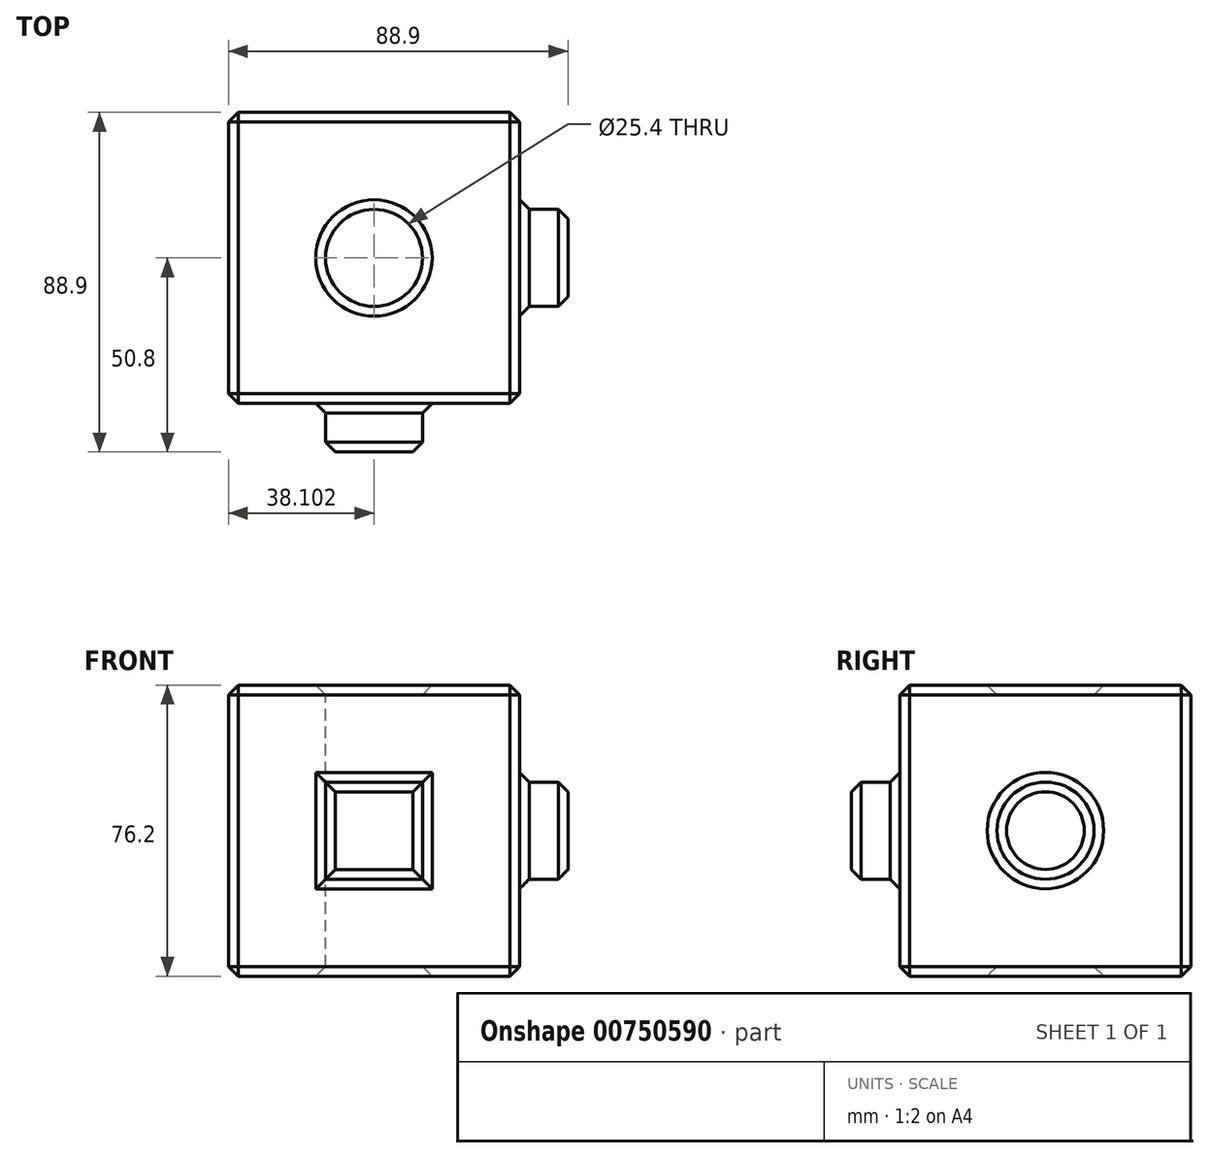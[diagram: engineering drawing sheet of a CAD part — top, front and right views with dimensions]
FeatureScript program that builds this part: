
annotation { "Feature Type Name" : "Feature", "Feature Type Description" : "" }
export const myFeature = defineFeature(function(context is Context, id is Id, definition is map)
    precondition{}
    {
        {
            var Q0;
            Q0=qCreatedBy(makeId("Front.planeOp"),FACE);
            var sketch = newSketch(context, id + "F0", { "sketchPlane" : qUnion([Q0])});
            skLineSegment(sketch, "E0.bottom", {"start": v(-35.36, -32.41) * mm, "end": v(40.84, -32.41) * mm});
            skLineSegment(sketch, "E0.top", {"start": v(-35.36, 43.79) * mm, "end": v(40.84, 43.79) * mm});
            skLineSegment(sketch, "E0.left", {"start": v(-35.36, -32.41) * mm, "end": v(-35.36, 43.79) * mm});
            skLineSegment(sketch, "E0.right", {"start": v(40.84, -32.41) * mm, "end": v(40.84, 43.79) * mm});
            skSolve(sketch);
        }
        {
            var Q0;
            Q0=makeQuery(id+"F0.imprint","IMPRINT",FACE,{"disambiguationData":[TD([[makeQuery(id+"F0.imprint","IMPRINT",EDGE,{"derivedFrom":sQuery(id+"F0.wireOp",EDGE,"E0.bottom")}),1.0]])]});
            extrude(context, id + "F1", {"entities" : qUnion([Q0]), "oppositeDirection" : true, "depth" : 76.2 * mm, "offsetDistance" : 25.4 * mm});
        }
        {
            var Q0;
            Q0=makeQuery(id+"F1.opExtrude","CAP_FACE",FACE,{"disambiguationData":[OSD([sQuery(id+"F0.wireOp",EDGE,"E0.bottom"),sQuery(id+"F0.wireOp",EDGE,"E0.top"),sQuery(id+"F0.wireOp",EDGE,"E0.left"),sQuery(id+"F0.wireOp",EDGE,"E0.right")])],"isStart":true});
            var sketch = newSketch(context, id + "F2", { "sketchPlane" : qUnion([Q0])});
            skLineSegment(sketch, "E1.bottom", {"start": v(-9.96, -7.01) * mm, "end": v(15.44, -7.01) * mm});
            skLineSegment(sketch, "E1.top", {"start": v(-9.96, 18.39) * mm, "end": v(15.44, 18.39) * mm});
            skLineSegment(sketch, "E1.left", {"start": v(-9.96, -7.01) * mm, "end": v(-9.96, 18.39) * mm});
            skLineSegment(sketch, "E1.right", {"start": v(15.44, -7.01) * mm, "end": v(15.44, 18.39) * mm});
            skSolve(sketch);
        }
        {
            var Q0;
            Q0=makeQuery(id+"F2.imprint","IMPRINT",FACE,{"disambiguationData":[TD([[makeQuery(id+"F2.imprint","IMPRINT",EDGE,{"derivedFrom":sQuery(id+"F2.wireOp",EDGE,"E1.bottom")}),1.0]])]});
            extrude(context, id + "F3", {"entities" : qUnion([Q0]), "operationType" : NewBodyOperationType.ADD, "depth" : 12.7 * mm, "offsetDistance" : 25.4 * mm});
        }
        {
            var Q0;
            Q0=makeQuery(id+"F1.opExtrude","SWEPT_FACE",FACE,{"disambiguationData":[OSD([sQuery(id+"F0.wireOp",EDGE,"E0.right")])]});
            var sketch = newSketch(context, id + "F4", { "sketchPlane" : qUnion([Q0])});
            skCircle(sketch, "E2", {"center": v(38.1, 5.69) * mm, "radius": 12.7 * mm});
            skSolve(sketch);
        }
        {
            var Q0;
            Q0=makeQuery(id+"F4.imprint","IMPRINT",FACE,{"disambiguationData":[TD([[makeQuery(id+"F4.imprint","IMPRINT",EDGE,{"derivedFrom":sQuery(id+"F4.wireOp",EDGE,"E2")}),1.0]])]});
            extrude(context, id + "F5", {"entities" : qUnion([Q0]), "operationType" : NewBodyOperationType.ADD, "depth" : 12.7 * mm, "offsetDistance" : 25.4 * mm});
        }
        {
            var Q0;
            Q0=makeQuery(id+"F1.opExtrude","SWEPT_FACE",FACE,{"disambiguationData":[OSD([sQuery(id+"F0.wireOp",EDGE,"E0.top")])]});
            var sketch = newSketch(context, id + "F6", { "sketchPlane" : qUnion([Q0])});
            skPoint(sketch, "E3", {"position": v(2.74, 38.1) * mm});
            skSolve(sketch);
        }
        {
            var Q0;
            Q0=sQuery(id+"F6.wireOp",VERTEX,"E3");
            var Q1;
            Q1=makeQuery(id+"F1.opExtrude","SWEPT_BODY",BODY,{"disambiguationData":[OSD([sQuery(id+"F0.wireOp",EDGE,"E0.bottom"),sQuery(id+"F0.wireOp",EDGE,"E0.top"),sQuery(id+"F0.wireOp",EDGE,"E0.left"),sQuery(id+"F0.wireOp",EDGE,"E0.right")])]});
            hole(context, id + "F7", {"style" : HoleStyle.SIMPLE, "endStyle" : HoleEndStyle.THROUGH, "holeDiameter" : 25.4 * mm, "majorDiameter" : 6.35 * mm, "isTappedThrough" : true, "tappedDepth" : 12.7 * mm, "tapClearance" : 3, "locations" : qUnion([Q0]), "scope" : qUnion([Q1])});
        }
        {
            var Q0;
            Q0=makeQuery(id+"F1.opExtrude","SWEPT_FACE",FACE,{"disambiguationData":[OSD([sQuery(id+"F0.wireOp",EDGE,"E0.top")])]});
            var Q1;
            Q1=makeQuery(id+"F3.opExtrude","CAP_FACE",FACE,{"disambiguationData":[OSD([sQuery(id+"F2.wireOp",EDGE,"E1.bottom"),sQuery(id+"F2.wireOp",EDGE,"E1.top"),sQuery(id+"F2.wireOp",EDGE,"E1.left"),sQuery(id+"F2.wireOp",EDGE,"E1.right")])],"isStart":false});
            var Q2;
            Q2=makeQuery(id+"F1.opExtrude","CAP_FACE",FACE,{"disambiguationData":[OSD([sQuery(id+"F0.wireOp",EDGE,"E0.bottom"),sQuery(id+"F0.wireOp",EDGE,"E0.top"),sQuery(id+"F0.wireOp",EDGE,"E0.left"),sQuery(id+"F0.wireOp",EDGE,"E0.right")])],"isStart":true});
            var Q3;
            Q3=makeQuery(id+"F1.opExtrude","SWEPT_FACE",FACE,{"disambiguationData":[OSD([sQuery(id+"F0.wireOp",EDGE,"E0.right")])]});
            var Q4;
            Q4=makeQuery(id+"F5.opExtrude","CAP_FACE",FACE,{"disambiguationData":[OSD([sQuery(id+"F4.wireOp",EDGE,"E2")])],"isStart":false});
            var Q5;
            Q5=makeQuery(id+"F1.opExtrude","CAP_FACE",FACE,{"disambiguationData":[OSD([sQuery(id+"F0.wireOp",EDGE,"E0.bottom"),sQuery(id+"F0.wireOp",EDGE,"E0.top"),sQuery(id+"F0.wireOp",EDGE,"E0.left"),sQuery(id+"F0.wireOp",EDGE,"E0.right")])],"isStart":false});
            var Q6;
            Q6=makeQuery(id+"F1.opExtrude","SWEPT_FACE",FACE,{"disambiguationData":[OSD([sQuery(id+"F0.wireOp",EDGE,"E0.bottom")])]});
            var Q7;
            Q7=makeQuery(id+"F1.opExtrude","SWEPT_FACE",FACE,{"disambiguationData":[OSD([sQuery(id+"F0.wireOp",EDGE,"E0.left")])]});
            chamfer(context, id + "F8", {"entities" : qUnion([Q0, Q1, Q2, Q3, Q4, Q5, Q6, Q7]), "width" : 2.54 * mm, "tangentPropagation" : true});
        }
    });
